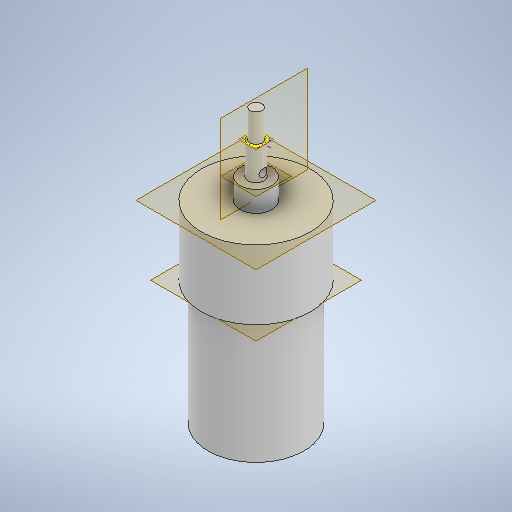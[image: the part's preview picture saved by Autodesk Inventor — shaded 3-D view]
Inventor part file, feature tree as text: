
AUTODESK INVENTOR PART (.ipt)
format: ipt  version: 2025.2 (Build 292293000, 293)  size: 286,208 bytes
history: native  units: mm
features: sketch x7, extrude x5, other x5, hole x1
ambient origin geometry x8: Origin, YZ Plane, XZ Plane, XY Plane, X Axis, Y Axis, Z Axis, Center Point
bodies: Body1 (feature_tree)
feature tree (18):
  extrude  "押し出し6"  Depth=24.0mm
  other  "作業平面4"
  extrude  "押し出し7"  Depth=31.0mm TaperAngle=0.0deg
  other  "作業平面5"
  extrude  "押し出し8"  TaperAngle=0.0deg  [1 undecoded]
  other  "作業平面6"
  extrude  "押し出し9"  Depth=27.3mm
  other  "作業平面7"
  extrude  "押し出し10"  Depth=17.3mm TaperAngle=0.0deg
  sketch  "スケッチ13"
  other  "作業平面8"
  hole  "穴2"  [1 undecoded]
  sketch  "スケッチ8"
  sketch  "スケッチ9"
  sketch  "スケッチ10"
  sketch  "スケッチ11"
  sketch  "スケッチ12"
  sketch  "スケッチ14"
note: 2 required parameter values undecoded (feature->parameter linkage not recoverable at this tier; creation-order binding heuristic only, values carry confidence <= 0.55)
